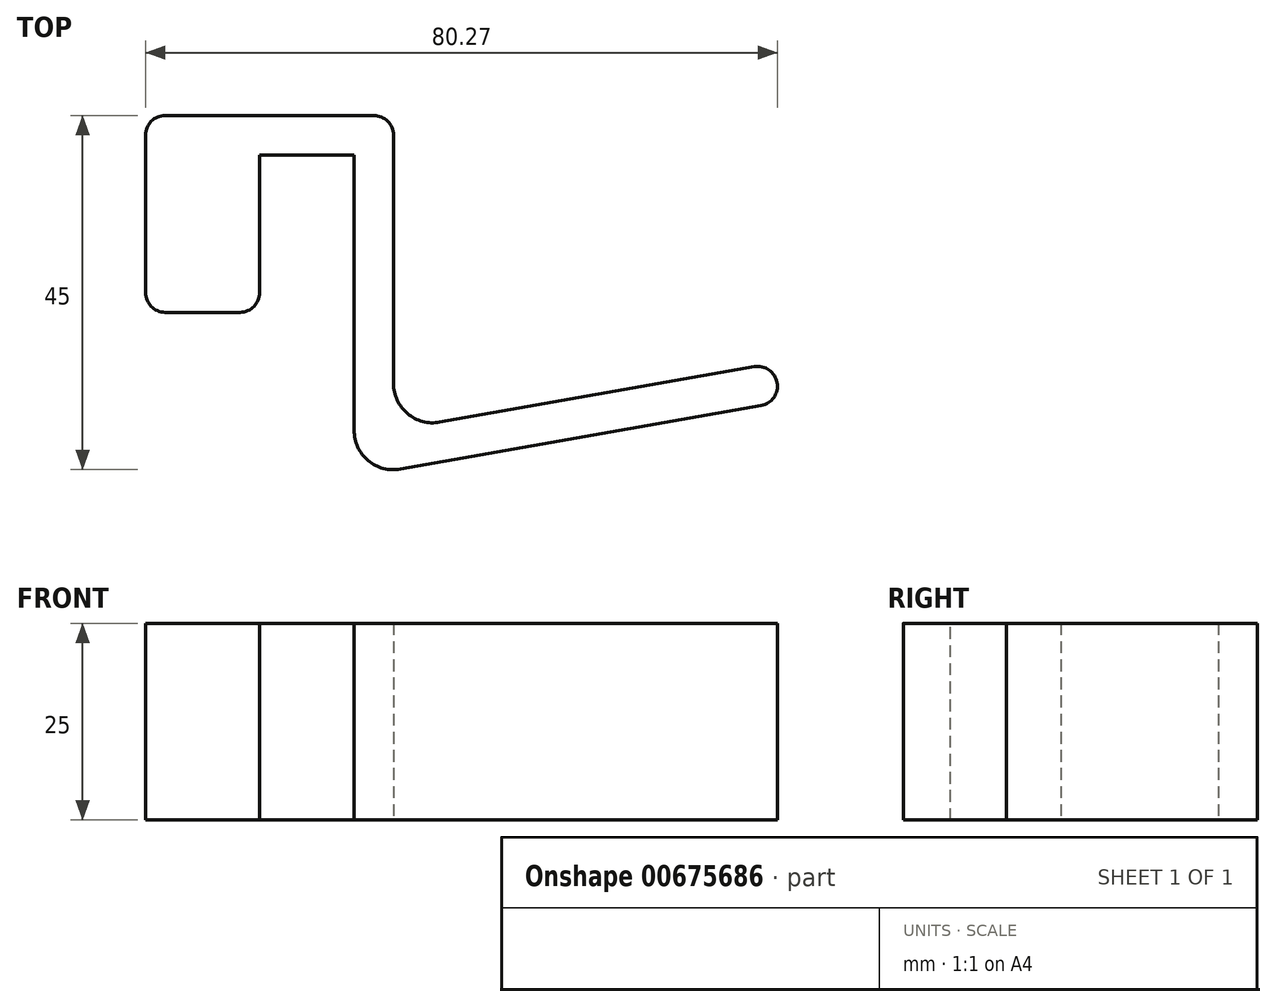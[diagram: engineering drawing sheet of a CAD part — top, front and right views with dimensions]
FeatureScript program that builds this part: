
annotation { "Feature Type Name" : "Feature", "Feature Type Description" : "" }
export const myFeature = defineFeature(function(context is Context, id is Id, definition is map)
    precondition{}
    {
        {
            var Q0;
            Q0=qCreatedBy(makeId("Top.planeOp"),FACE);
            var sketch = newSketch(context, id + "F0", { "sketchPlane" : qUnion([Q0])});
            skLineSegment(sketch, "E0", {"start": v(0, 0) * mm, "end": v(0, 25) * mm});
            skLineSegment(sketch, "E1", {"start": v(0, 25) * mm, "end": v(31.5, 25) * mm});
            skLineSegment(sketch, "E2", {"start": v(31.5, 25) * mm, "end": v(31.5, -15) * mm});
            skLineSegment(sketch, "E3", {"start": v(0, 0) * mm, "end": v(14.5, 0) * mm});
            skLineSegment(sketch, "E4", {"start": v(14.5, 0) * mm, "end": v(14.5, 20) * mm});
            skLineSegment(sketch, "E5", {"start": v(14.5, 20) * mm, "end": v(26.5, 20) * mm});
            skLineSegment(sketch, "E6", {"start": v(31.5, -15) * mm, "end": v(79.8, -6.48) * mm});
            skLineSegment(sketch, "E7", {"start": v(79.8, -6.48) * mm, "end": v(80.66, -11.4) * mm});
            skLineSegment(sketch, "E8", {"start": v(26.5, 20) * mm, "end": v(26.5, -20.96) * mm});
            skLineSegment(sketch, "E9", {"start": v(80.66, -11.4) * mm, "end": v(26.5, -20.96) * mm});
            skSolve(sketch);
        }
        {
            var Q0;
            Q0 = qSketchRegion(id + "F0", true);
            extrude(context, id + "F1", {"entities" : qUnion([Q0]), "depth" : 25 * mm, "offsetDistance" : 25 * mm});
        }
        {
            var Q0;
            Q0=qCreatedBy(makeId("Top.planeOp"),FACE);
            var sketch = newSketch(context, id + "F2", { "sketchPlane" : qUnion([Q0])});
            skLineSegment(sketch, "E10.bottom", {"start": v(0, 0) * mm, "end": v(14.5, 0) * mm});
            skLineSegment(sketch, "E10.top", {"start": v(0, 25) * mm, "end": v(14.5, 25) * mm});
            skLineSegment(sketch, "E10.left", {"start": v(0, 0) * mm, "end": v(0, 25) * mm});
            skLineSegment(sketch, "E10.right", {"start": v(14.5, 0) * mm, "end": v(14.5, 25) * mm});
            skSolve(sketch);
        }
        {
            var Q0;
            Q0=makeQuery(id+"F1.opExtrude","SWEPT_EDGE",EDGE,{"disambiguationData":[OSD([sQuery(id+"F0.wireOp",EDGE,"E8"),sQuery(id+"F0.wireOp",EDGE,"E9")])]});
            var Q1;
            Q1=makeQuery(id+"F1.opExtrude","SWEPT_EDGE",EDGE,{"disambiguationData":[OSD([sQuery(id+"F0.wireOp",EDGE,"E2"),sQuery(id+"F0.wireOp",EDGE,"E6")])]});
            fillet(context, id + "F3", {"entities" : qUnion([Q0, Q1]), "radius" : 5 * mm, "tangentPropagation" : true, "allowEdgeOverflow" : false});
        }
        {
            var Q0;
            Q0=makeQuery(id+"FXIPMbZC7L2q240_1.boolean.opBoolean","MERGE",EDGE,{"derivedFrom":[makeQuery(id+"F1.opExtrude","SWEPT_EDGE",EDGE,{"disambiguationData":[OSD([sQuery(id+"F0.wireOp",EDGE,"E0"),sQuery(id+"F0.wireOp",EDGE,"E1")])]}),makeQuery(id+"FXIPMbZC7L2q240_1.opExtrude","SWEPT_EDGE",EDGE,{"disambiguationData":[OSD([sQuery(id+"F2.wireOp",EDGE,"E10.top"),sQuery(id+"F2.wireOp",EDGE,"E10.left")])]})]});
            var Q1;
            Q1=makeQuery(id+"FXIPMbZC7L2q240_1.boolean.opBoolean","MERGE",EDGE,{"derivedFrom":[makeQuery(id+"F1.opExtrude","SWEPT_EDGE",EDGE,{"disambiguationData":[OSD([sQuery(id+"F0.wireOp",EDGE,"E0"),sQuery(id+"F0.wireOp",EDGE,"E3")])]}),makeQuery(id+"FXIPMbZC7L2q240_1.opExtrude","SWEPT_EDGE",EDGE,{"disambiguationData":[OSD([sQuery(id+"F2.wireOp",EDGE,"E10.bottom"),sQuery(id+"F2.wireOp",EDGE,"E10.left")])]})]});
            var Q2;
            Q2=makeQuery(id+"FXIPMbZC7L2q240_1.boolean.opBoolean","MERGE",EDGE,{"derivedFrom":[makeQuery(id+"F1.opExtrude","SWEPT_EDGE",EDGE,{"disambiguationData":[OSD([sQuery(id+"F0.wireOp",EDGE,"E3"),sQuery(id+"F0.wireOp",EDGE,"E4")])]}),makeQuery(id+"FXIPMbZC7L2q240_1.opExtrude","SWEPT_EDGE",EDGE,{"disambiguationData":[OSD([sQuery(id+"F2.wireOp",EDGE,"E10.bottom"),sQuery(id+"F2.wireOp",EDGE,"E10.right")])]})]});
            var Q3;
            Q3=makeQuery(id+"FXIPMbZC7L2q240_1.opExtrude","SWEPT_EDGE",EDGE,{"disambiguationData":[OSD([sQuery(id+"F2.wireOp",EDGE,"E10.top"),sQuery(id+"F2.wireOp",EDGE,"E10.right")])]});
            var Q4;
            Q4=makeQuery(id+"F1.opExtrude","SWEPT_EDGE",EDGE,{"disambiguationData":[OSD([sQuery(id+"F0.wireOp",EDGE,"E1"),sQuery(id+"F0.wireOp",EDGE,"E2")])]});
            var Q5;
            Q5=makeQuery(id+"F1.opExtrude","SWEPT_EDGE",EDGE,{"disambiguationData":[OSD([sQuery(id+"F0.wireOp",EDGE,"E6"),sQuery(id+"F0.wireOp",EDGE,"E7")])]});
            var Q6;
            Q6=makeQuery(id+"F1.opExtrude","SWEPT_EDGE",EDGE,{"disambiguationData":[OSD([sQuery(id+"F0.wireOp",EDGE,"E7"),sQuery(id+"F0.wireOp",EDGE,"E9")])]});
            fillet(context, id + "F4", {"entities" : qUnion([Q0, Q1, Q2, Q3, Q4, Q5, Q6]), "radius" : 2.5 * mm, "tangentPropagation" : true, "allowEdgeOverflow" : false});
        }
    });
